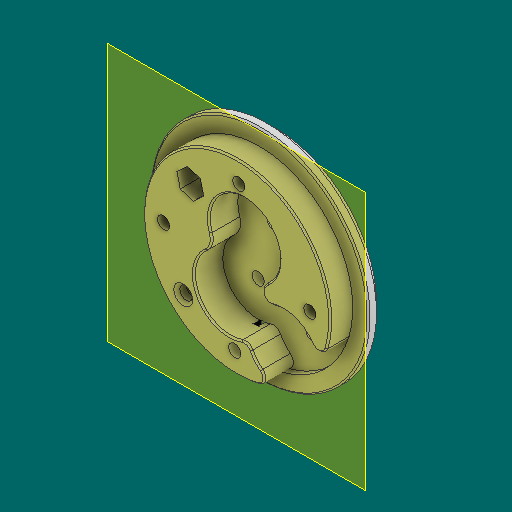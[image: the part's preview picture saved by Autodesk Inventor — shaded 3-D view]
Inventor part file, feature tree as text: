
AUTODESK INVENTOR PART (.ipt)
format: ipt  version: 2023.1 (Build 271208000, 208)  size: 268,288 bytes
history: native  units: in
note: dims shown in document units (in); Inventor stores cm internally (conversion verified against a paired STEP export)
features: sketch x6, other x3, plane x1
ambient origin geometry x8: Origin, YZ Plane, XZ Plane, XY Plane, X Axis, Y Axis, Z Axis, Center Point
bodies: Solid1 (feature_tree)
feature tree (10):
  other  "DiffCap.ipt"
  other  "Solid1::DiffCap.ipt"
  other  "TaggingFeature1"
  sketch  "Sketch1"  dims[d0=0.3937in]
  sketch  "Sketch2"
  sketch  "Sketch3"
  sketch  "Sketch4"
  sketch  "Sketch5"
  sketch  "Sketch6"
  plane  "Work Plane1"
